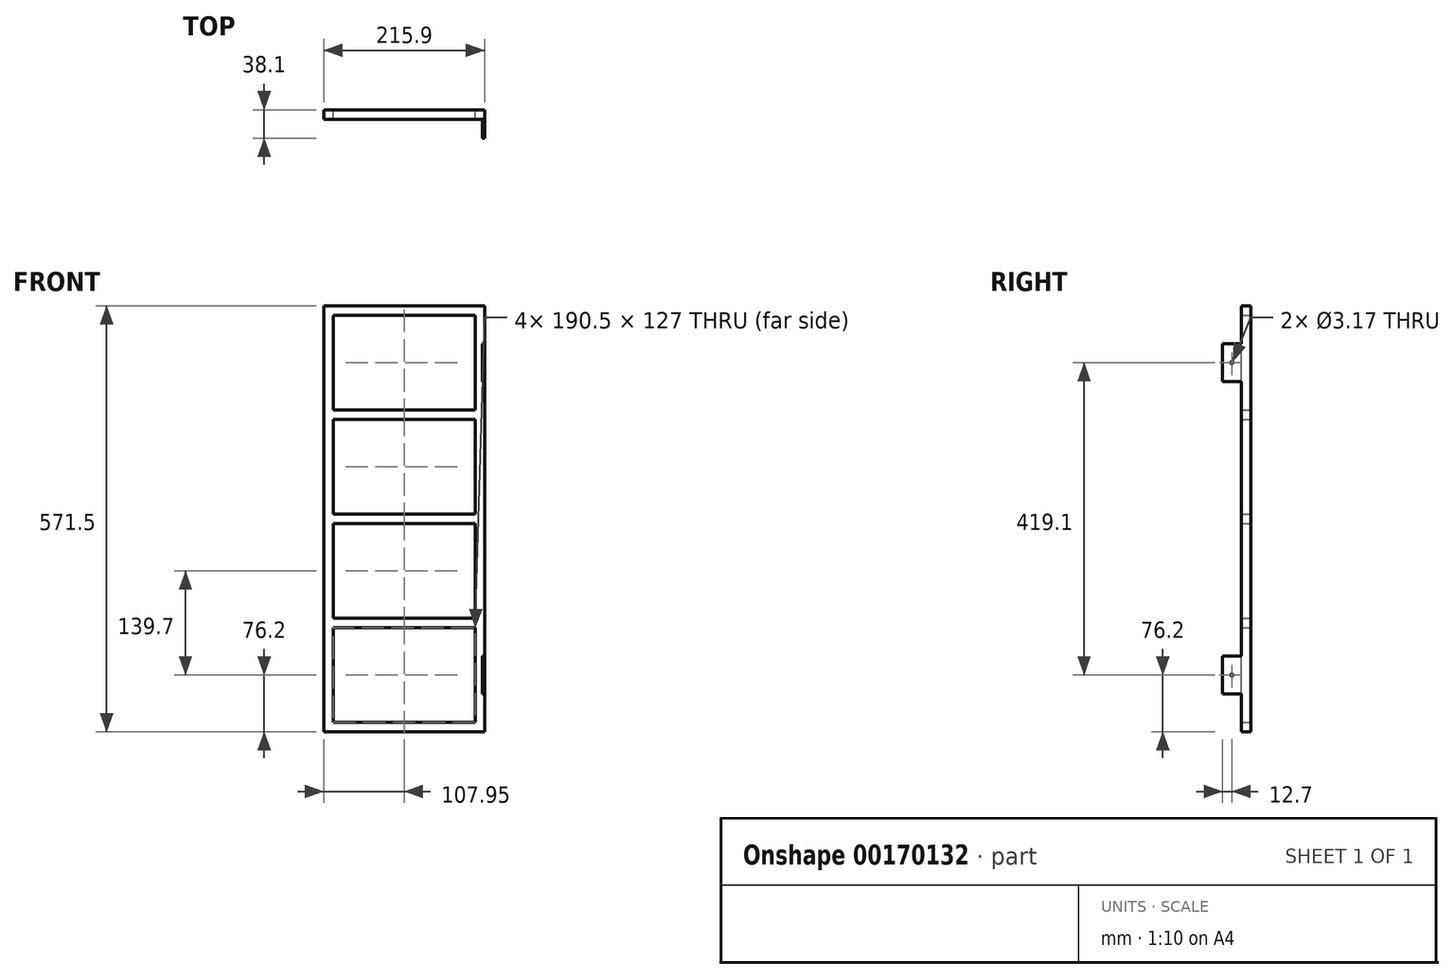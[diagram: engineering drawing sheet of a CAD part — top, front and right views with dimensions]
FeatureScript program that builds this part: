
annotation { "Feature Type Name" : "Feature", "Feature Type Description" : "" }
export const myFeature = defineFeature(function(context is Context, id is Id, definition is map)
    precondition{}
    {
        {
            var Q0;
            Q0=qCreatedBy(makeId("Front.planeOp"),FACE);
            var sketch = newSketch(context, id + "F0", { "sketchPlane" : qUnion([Q0])});
            skLineSegment(sketch, "E0.bottom", {"start": v(0, 0) * mm, "end": v(215.9, 0) * mm});
            skLineSegment(sketch, "E0.left", {"start": v(0, 0) * mm, "end": v(0, 571.5) * mm});
            skLineSegment(sketch, "E0.right", {"start": v(215.9, 0) * mm, "end": v(215.9, 571.5) * mm});
            skLineSegment(sketch, "E1.bottom", {"start": v(12.7, 12.7) * mm, "end": v(203.2, 12.7) * mm});
            skLineSegment(sketch, "E1.left", {"start": v(12.7, 12.7) * mm, "end": v(12.7, 139.7) * mm});
            skLineSegment(sketch, "E1.right", {"start": v(203.2, 12.7) * mm, "end": v(203.2, 139.7) * mm});
            skLineSegment(sketch, "E2.bottom", {"start": v(12.7, 152.4) * mm, "end": v(203.2, 152.4) * mm});
            skLineSegment(sketch, "E2.top", {"start": v(12.7, 139.7) * mm, "end": v(203.2, 139.7) * mm});
            skLineSegment(sketch, "E3.bottom", {"start": v(12.7, 292.1) * mm, "end": v(203.2, 292.1) * mm});
            skLineSegment(sketch, "E3.top", {"start": v(12.7, 279.4) * mm, "end": v(203.2, 279.4) * mm});
            skLineSegment(sketch, "E4.bottom", {"start": v(12.7, 431.8) * mm, "end": v(203.2, 431.8) * mm});
            skLineSegment(sketch, "E4.top", {"start": v(12.7, 419.1) * mm, "end": v(203.2, 419.1) * mm});
            skLineSegment(sketch, "E5.bottom", {"start": v(12.7, 571.5) * mm, "end": v(203.2, 571.5) * mm});
            skLineSegment(sketch, "E5.top", {"start": v(12.7, 558.8) * mm, "end": v(203.2, 558.8) * mm});
            skLineSegment(sketch, "E6.trimOffspring", {"start": v(203.2, 431.8) * mm, "end": v(203.2, 558.8) * mm});
            skLineSegment(sketch, "E7.trimOffspring", {"start": v(12.7, 431.8) * mm, "end": v(12.7, 558.8) * mm});
            skLineSegment(sketch, "E8.trimOffspring", {"start": v(203.2, 292.1) * mm, "end": v(203.2, 419.1) * mm});
            skLineSegment(sketch, "E9.trimOffspring", {"start": v(12.7, 292.1) * mm, "end": v(12.7, 419.1) * mm});
            skLineSegment(sketch, "E10.trimOffspring", {"start": v(12.7, 152.4) * mm, "end": v(12.7, 279.4) * mm});
            skLineSegment(sketch, "E11.trimOffspring", {"start": v(203.2, 152.4) * mm, "end": v(203.2, 279.4) * mm});
            skLineSegment(sketch, "E12", {"start": v(0, 571.5) * mm, "end": v(215.9, 571.5) * mm});
            skSolve(sketch);
        }
        {
            var Q0;
            Q0=makeQuery(id+"F0.imprint","IMPRINT",FACE,{"disambiguationData":[TD([[makeQuery(id+"F0.imprint","IMPRINT",EDGE,{"derivedFrom":sQuery(id+"F0.wireOp",EDGE,"E0.bottom")}),1.0]])]});
            extrude(context, id + "F1", {"entities" : qUnion([Q0]), "depth" : 12.7 * mm});
        }
        {
            var Q0;
            Q0=makeQuery(id+"F1.opExtrude","CAP_FACE",FACE,{"disambiguationData":[OSD([sQuery(id+"F0.wireOp",EDGE,"E0.bottom"),sQuery(id+"F0.wireOp",EDGE,"E0.left"),sQuery(id+"F0.wireOp",EDGE,"E0.right"),sQuery(id+"F0.wireOp",EDGE,"E1.bottom"),sQuery(id+"F0.wireOp",EDGE,"E1.left"),sQuery(id+"F0.wireOp",EDGE,"E1.right"),sQuery(id+"F0.wireOp",EDGE,"E2.bottom"),sQuery(id+"F0.wireOp",EDGE,"E2.top"),sQuery(id+"F0.wireOp",EDGE,"E3.bottom"),sQuery(id+"F0.wireOp",EDGE,"E3.top"),sQuery(id+"F0.wireOp",EDGE,"E4.bottom"),sQuery(id+"F0.wireOp",EDGE,"E4.top"),sQuery(id+"F0.wireOp",EDGE,"E5.top"),sQuery(id+"F0.wireOp",EDGE,"E6.trimOffspring"),sQuery(id+"F0.wireOp",EDGE,"E7.trimOffspring"),sQuery(id+"F0.wireOp",EDGE,"E8.trimOffspring"),sQuery(id+"F0.wireOp",EDGE,"E9.trimOffspring"),sQuery(id+"F0.wireOp",EDGE,"E10.trimOffspring"),sQuery(id+"F0.wireOp",EDGE,"E11.trimOffspring"),sQuery(id+"F0.wireOp",EDGE,"E12")])],"isStart":false});
            var sketch = newSketch(context, id + "F2", { "sketchPlane" : qUnion([Q0])});
            skLineSegment(sketch, "E13.bottom", {"start": v(215.9, 520.7) * mm, "end": v(212.72, 520.7) * mm});
            skLineSegment(sketch, "E13.top", {"start": v(215.9, 469.9) * mm, "end": v(212.72, 469.9) * mm});
            skLineSegment(sketch, "E13.left", {"start": v(215.9, 520.7) * mm, "end": v(215.9, 469.9) * mm});
            skLineSegment(sketch, "E13.right", {"start": v(212.72, 520.7) * mm, "end": v(212.72, 469.9) * mm});
            skSolve(sketch);
        }
        {
            var Q0;
            Q0 = qSketchRegion(id + "F2", true);
            extrude(context, id + "F3", {"entities" : qUnion([Q0]), "operationType" : NewBodyOperationType.ADD, "depth" : 25.4 * mm});
        }
        {
            var Q0;
            Q0=makeQuery(id+"F1.opExtrude","CAP_FACE",FACE,{"disambiguationData":[OSD([sQuery(id+"F0.wireOp",EDGE,"E0.bottom"),sQuery(id+"F0.wireOp",EDGE,"E0.left"),sQuery(id+"F0.wireOp",EDGE,"E0.right"),sQuery(id+"F0.wireOp",EDGE,"E1.bottom"),sQuery(id+"F0.wireOp",EDGE,"E1.left"),sQuery(id+"F0.wireOp",EDGE,"E1.right"),sQuery(id+"F0.wireOp",EDGE,"E2.bottom"),sQuery(id+"F0.wireOp",EDGE,"E2.top"),sQuery(id+"F0.wireOp",EDGE,"E3.bottom"),sQuery(id+"F0.wireOp",EDGE,"E3.top"),sQuery(id+"F0.wireOp",EDGE,"E4.bottom"),sQuery(id+"F0.wireOp",EDGE,"E4.top"),sQuery(id+"F0.wireOp",EDGE,"E5.top"),sQuery(id+"F0.wireOp",EDGE,"E6.trimOffspring"),sQuery(id+"F0.wireOp",EDGE,"E7.trimOffspring"),sQuery(id+"F0.wireOp",EDGE,"E8.trimOffspring"),sQuery(id+"F0.wireOp",EDGE,"E9.trimOffspring"),sQuery(id+"F0.wireOp",EDGE,"E10.trimOffspring"),sQuery(id+"F0.wireOp",EDGE,"E11.trimOffspring"),sQuery(id+"F0.wireOp",EDGE,"E12")])],"isStart":false});
            var sketch = newSketch(context, id + "F4", { "sketchPlane" : qUnion([Q0])});
            skLineSegment(sketch, "E14.bottom", {"start": v(215.9, 101.6) * mm, "end": v(212.72, 101.6) * mm});
            skLineSegment(sketch, "E14.top", {"start": v(215.9, 50.8) * mm, "end": v(212.72, 50.8) * mm});
            skLineSegment(sketch, "E14.left", {"start": v(215.9, 101.6) * mm, "end": v(215.9, 50.8) * mm});
            skLineSegment(sketch, "E14.right", {"start": v(212.73, 101.6) * mm, "end": v(212.73, 50.8) * mm});
            skSolve(sketch);
        }
        {
            var Q0;
            Q0 = qSketchRegion(id + "F4", true);
            extrude(context, id + "F5", {"entities" : qUnion([Q0]), "operationType" : NewBodyOperationType.ADD, "depth" : 25.4 * mm});
        }
        {
            var Q0;
            Q0=makeQuery(id+"F3.opExtrude","SWEPT_FACE",FACE,{"disambiguationData":[OSD([sQuery(id+"F2.wireOp",EDGE,"E13.right")])]});
            var sketch = newSketch(context, id + "F6", { "sketchPlane" : qUnion([Q0])});
            skPoint(sketch, "E15", {"position": v(25.4, 495.3) * mm});
            skPoint(sketch, "E15.positionSnap0", {"position": v(12.7, 495.3) * mm});
            skPoint(sketch, "E16", {"position": v(25.4, 76.2) * mm});
            skSolve(sketch);
        }
        {
            var Q0;
            Q0=sQuery(id+"F6.wireOp",VERTEX,"E15");
            var Q1;
            Q1=sQuery(id+"F6.wireOp",VERTEX,"E16");
            var Q2;
            Q2=makeQuery(id+"F1.opExtrude","SWEPT_BODY",BODY,{"disambiguationData":[OSD([sQuery(id+"F0.wireOp",EDGE,"E0.bottom"),sQuery(id+"F0.wireOp",EDGE,"E0.left"),sQuery(id+"F0.wireOp",EDGE,"E0.right"),sQuery(id+"F0.wireOp",EDGE,"E1.bottom"),sQuery(id+"F0.wireOp",EDGE,"E1.left"),sQuery(id+"F0.wireOp",EDGE,"E1.right"),sQuery(id+"F0.wireOp",EDGE,"E2.bottom"),sQuery(id+"F0.wireOp",EDGE,"E2.top"),sQuery(id+"F0.wireOp",EDGE,"E3.bottom"),sQuery(id+"F0.wireOp",EDGE,"E3.top"),sQuery(id+"F0.wireOp",EDGE,"E4.bottom"),sQuery(id+"F0.wireOp",EDGE,"E4.top"),sQuery(id+"F0.wireOp",EDGE,"E5.top"),sQuery(id+"F0.wireOp",EDGE,"E6.trimOffspring"),sQuery(id+"F0.wireOp",EDGE,"E7.trimOffspring"),sQuery(id+"F0.wireOp",EDGE,"E8.trimOffspring"),sQuery(id+"F0.wireOp",EDGE,"E9.trimOffspring"),sQuery(id+"F0.wireOp",EDGE,"E10.trimOffspring"),sQuery(id+"F0.wireOp",EDGE,"E11.trimOffspring"),sQuery(id+"F0.wireOp",EDGE,"E12")])]});
            hole(context, id + "F7", {"style" : HoleStyle.SIMPLE, "endStyle" : HoleEndStyle.THROUGH, "holeDiameter" : 3.17 * mm, "locations" : qUnion([Q0, Q1]), "scope" : qUnion([Q2]), "isTappedThrough" : true});
        }
    });
